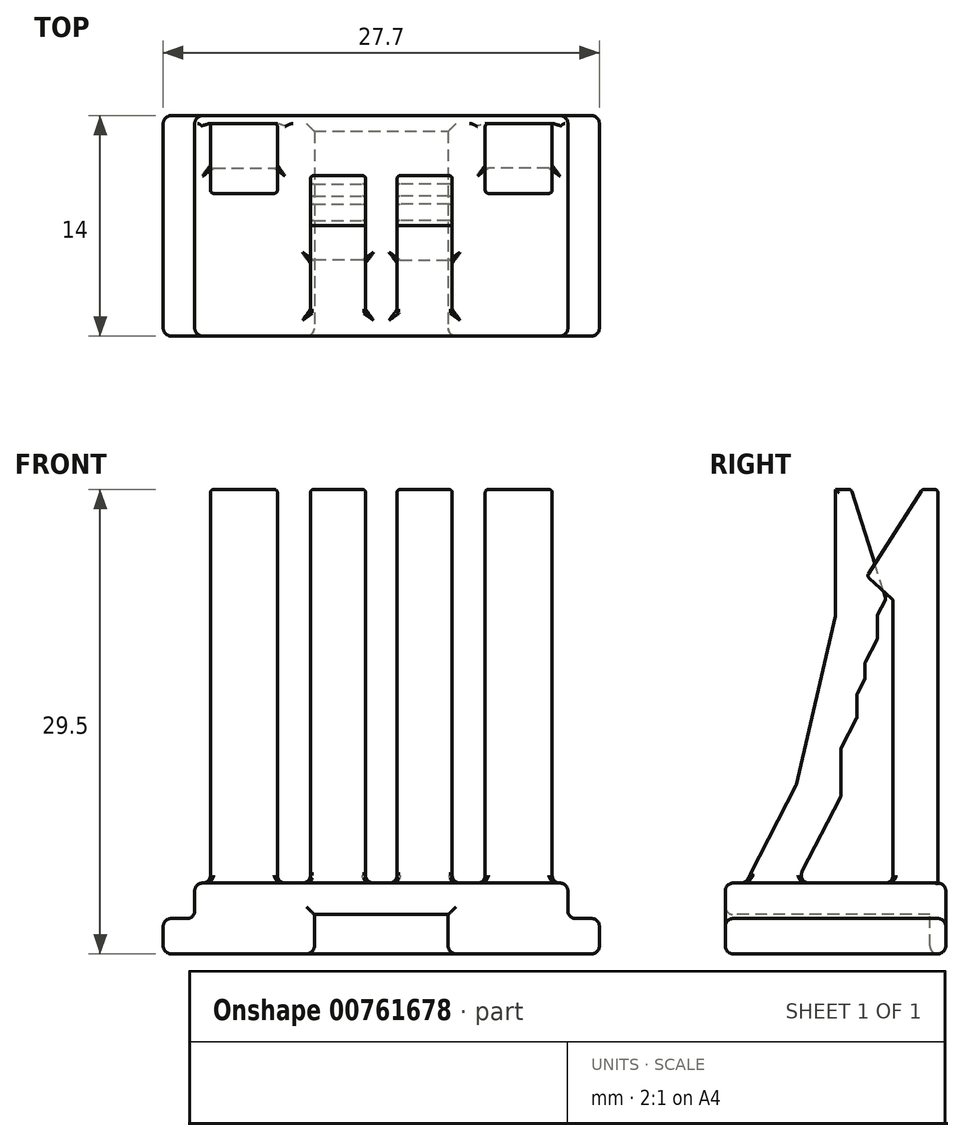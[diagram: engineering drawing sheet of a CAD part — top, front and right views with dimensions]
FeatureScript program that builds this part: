
annotation { "Feature Type Name" : "Feature", "Feature Type Description" : "" }
export const myFeature = defineFeature(function(context is Context, id is Id, definition is map)
    precondition{}
    {
        {
            var Q0;
            Q0=qCreatedBy(makeId("Front.planeOp"),FACE);
            var sketch = newSketch(context, id + "F0", { "sketchPlane" : qUnion([Q0])});
            skLineSegment(sketch, "E0.bottom", {"start": v(-13.85, -2.25) * mm, "end": v(13.85, -2.25) * mm});
            skLineSegment(sketch, "E0.top", {"start": v(-13.85, 2.25) * mm, "end": v(13.85, 2.25) * mm});
            skLineSegment(sketch, "E0.left", {"start": v(-13.85, -2.25) * mm, "end": v(-13.85, 2.25) * mm});
            skLineSegment(sketch, "E0.right", {"start": v(13.85, -2.25) * mm, "end": v(13.85, 2.25) * mm});
            skLineSegment(sketch, "E1", {"start": v(0, 2.25) * mm, "end": v(0, -2.25) * mm, "construction": true});
            skSolve(sketch);
        }
        {
            var Q0;
            Q0 = qSketchRegion(id + "F0", true);
            extrude(context, id + "F1", {"entities" : qUnion([Q0]), "endBound" : BoundingType.SYMMETRIC, "depth" : 14 * mm, "offsetDistance" : 25 * mm});
        }
        {
            var Q0;
            Q0=makeQuery(id+"F1.opExtrude","CAP_FACE",FACE,{"disambiguationData":[OSD([sQuery(id+"F0.wireOp",EDGE,"E0.bottom"),sQuery(id+"F0.wireOp",EDGE,"E0.top"),sQuery(id+"F0.wireOp",EDGE,"E0.left"),sQuery(id+"F0.wireOp",EDGE,"E0.right")])],"isStart":false});
            var sketch = newSketch(context, id + "F2", { "sketchPlane" : qUnion([Q0])});
            skLineSegment(sketch, "E2.bottom", {"start": v(-4.25, -2.25) * mm, "end": v(4.25, -2.25) * mm});
            skLineSegment(sketch, "E2.top", {"start": v(-4.25, 0.25) * mm, "end": v(4.25, 0.25) * mm});
            skLineSegment(sketch, "E2.left", {"start": v(-4.25, -2.25) * mm, "end": v(-4.25, 0.25) * mm});
            skLineSegment(sketch, "E2.right", {"start": v(4.25, -2.25) * mm, "end": v(4.25, 0.25) * mm});
            skSolve(sketch);
        }
        {
            var Q0;
            Q0 = qSketchRegion(id + "F2", true);
            extrude(context, id + "F3", {"entities" : qUnion([Q0]), "operationType" : NewBodyOperationType.REMOVE, "oppositeDirection" : true, "depth" : 13 * mm, "offsetDistance" : 25 * mm});
        }
        {
            var Q0;
            Q0=makeQuery(id+"F1.opExtrude","CAP_FACE",FACE,{"disambiguationData":[OSD([sQuery(id+"F0.wireOp",EDGE,"E0.bottom"),sQuery(id+"F0.wireOp",EDGE,"E0.top"),sQuery(id+"F0.wireOp",EDGE,"E0.left"),sQuery(id+"F0.wireOp",EDGE,"E0.right")])],"isStart":false});
            var sketch = newSketch(context, id + "F4", { "sketchPlane" : qUnion([Q0])});
            skLineSegment(sketch, "E3.bottom", {"start": v(-13.85, 2.25) * mm, "end": v(-11.85, 2.25) * mm});
            skLineSegment(sketch, "E3.top", {"start": v(-13.85, 0) * mm, "end": v(-11.85, 0) * mm});
            skLineSegment(sketch, "E3.left", {"start": v(-13.85, 2.25) * mm, "end": v(-13.85, 0) * mm});
            skLineSegment(sketch, "E3.right", {"start": v(-11.85, 2.25) * mm, "end": v(-11.85, 0) * mm});
            skLineSegment(sketch, "E4.bottom", {"start": v(13.85, 2.25) * mm, "end": v(11.85, 2.25) * mm});
            skLineSegment(sketch, "E4.top", {"start": v(13.85, 0) * mm, "end": v(11.85, 0) * mm});
            skLineSegment(sketch, "E4.left", {"start": v(13.85, 2.25) * mm, "end": v(13.85, 0) * mm});
            skLineSegment(sketch, "E4.right", {"start": v(11.85, 2.25) * mm, "end": v(11.85, 0) * mm});
            skSolve(sketch);
        }
        {
            var Q0;
            Q0 = qSketchRegion(id + "F4", true);
            extrude(context, id + "F5", {"entities" : qUnion([Q0]), "operationType" : NewBodyOperationType.REMOVE, "endBound" : BoundingType.UP_TO_NEXT, "oppositeDirection" : true, "depth" : 25 * mm, "offsetDistance" : 25 * mm});
        }
        {
            var Q0;
            Q0=qCreatedBy(makeId("Right.planeOp"),FACE);
            cPlane(context, id + "F6", {"entities" : qUnion([Q0]), "cplaneType" : CPlaneType.OFFSET, "offset" : 6.6 * mm, "width" : 150 * mm, "height" : 150 * mm});
        }
        {
            var Q0;
            Q0=qCreatedBy(id+"F6.planeOp",FACE);
            var sketch = newSketch(context, id + "F7", { "sketchPlane" : qUnion([Q0])});
            skLineSegment(sketch, "E5.bottom", {"start": v(6.5, 2.25) * mm, "end": v(3.65, 2.25) * mm});
            skLineSegment(sketch, "E5.left", {"start": v(6.5, 2.25) * mm, "end": v(6.5, 27.25) * mm});
            skLineSegment(sketch, "E5.right", {"start": v(3.65, 2.25) * mm, "end": v(3.65, 20.25) * mm});
            skLineSegment(sketch, "E6", {"start": v(3.65, 20.25) * mm, "end": v(2, 21.75) * mm});
            skLineSegment(sketch, "E7", {"start": v(2, 21.75) * mm, "end": v(5.5, 27.25) * mm});
            skLineSegment(sketch, "E8", {"start": v(5.5, 27.25) * mm, "end": v(6.5, 27.25) * mm});
            skSolve(sketch);
        }
        {
            var Q0;
            Q0 = qSketchRegion(id + "F7", true);
            extrude(context, id + "F8", {"entities" : qUnion([Q0]), "depth" : 4.25 * mm, "offsetDistance" : 25 * mm});
        }
        {
            var Q0;
            Q0=qCreatedBy(makeId("Right.planeOp"),FACE);
            cPlane(context, id + "F9", {"entities" : qUnion([Q0]), "cplaneType" : CPlaneType.OFFSET, "offset" : 1 * mm, "width" : 150 * mm, "height" : 150 * mm});
        }
        {
            var Q0;
            Q0=qCreatedBy(id+"F9.planeOp",FACE);
            var sketch = newSketch(context, id + "F10", { "sketchPlane" : qUnion([Q0])});
            skLineSegment(sketch, "E9", {"start": v(1.36, 12.75) * mm, "end": v(0.33, 10.75) * mm});
            skLineSegment(sketch, "E10", {"start": v(0.33, 10.75) * mm, "end": v(0.33, 7.75) * mm});
            skLineSegment(sketch, "E11", {"start": v(0.33, 7.75) * mm, "end": v(-2.5, 2.25) * mm});
            skLineSegment(sketch, "E12", {"start": v(-2.5, 2.25) * mm, "end": v(-5.7, 2.25) * mm});
            skLineSegment(sketch, "E13", {"start": v(-5.7, 2.25) * mm, "end": v(-2.5, 8.48) * mm});
            skLineSegment(sketch, "E14", {"start": v(1.36, 12.75) * mm, "end": v(1.36, 14.25) * mm});
            skLineSegment(sketch, "E15", {"start": v(1.36, 14.25) * mm, "end": v(1.88, 15.25) * mm});
            skLineSegment(sketch, "E16", {"start": v(1.88, 15.25) * mm, "end": v(1.88, 16.25) * mm});
            skLineSegment(sketch, "E17", {"start": v(1.88, 16.25) * mm, "end": v(2.65, 17.75) * mm});
            skLineSegment(sketch, "E18", {"start": v(2.65, 17.75) * mm, "end": v(2.65, 19.25) * mm});
            skLineSegment(sketch, "E19", {"start": v(2.65, 19.25) * mm, "end": v(3.2, 20.32) * mm});
            skLineSegment(sketch, "E20", {"start": v(3.2, 20.32) * mm, "end": v(1, 27.25) * mm});
            skLineSegment(sketch, "E21", {"start": v(1, 27.25) * mm, "end": v(0, 27.25) * mm});
            skLineSegment(sketch, "E22", {"start": v(0, 27.25) * mm, "end": v(0, 19.25) * mm});
            skLineSegment(sketch, "E23", {"start": v(0, 19.25) * mm, "end": v(-2.5, 8.48) * mm});
            skSolve(sketch);
        }
        {
            var Q0;
            Q0 = qSketchRegion(id + "F10", true);
            extrude(context, id + "F11", {"entities" : qUnion([Q0]), "depth" : 3.5 * mm, "offsetDistance" : 25 * mm});
        }
        {
            var Q0;
            Q0=makeQuery(id+"F1.opExtrude","CAP_FACE",FACE,{"disambiguationData":[OSD([sQuery(id+"F0.wireOp",EDGE,"E0.bottom"),sQuery(id+"F0.wireOp",EDGE,"E0.top"),sQuery(id+"F0.wireOp",EDGE,"E0.left"),sQuery(id+"F0.wireOp",EDGE,"E0.right")])],"isStart":false});
            var Q1;
            Q1=makeQuery(id+"F1.opExtrude","CAP_FACE",FACE,{"disambiguationData":[OSD([sQuery(id+"F0.wireOp",EDGE,"E0.bottom"),sQuery(id+"F0.wireOp",EDGE,"E0.top"),sQuery(id+"F0.wireOp",EDGE,"E0.left"),sQuery(id+"F0.wireOp",EDGE,"E0.right")])],"isStart":true});
            var Q2;
            Q2=makeQuery(id+"F1.opExtrude","SWEPT_FACE",FACE,{"disambiguationData":[OSD([sQuery(id+"F0.wireOp",EDGE,"E0.top")])]});
            var Q3;
            Q3=makeQuery(id+"F1.opExtrude","SWEPT_FACE",FACE,{"disambiguationData":[OSD([sQuery(id+"F0.wireOp",EDGE,"E0.bottom")])]});
            var Q4;
            Q4=makeQuery(id+"F5.boolean.opBoolean","COPY",FACE,{"derivedFrom":makeQuery(id+"F5.opExtrude","SWEPT_FACE",FACE,{"disambiguationData":[OSD([sQuery(id+"F4.wireOp",EDGE,"E3.top")])]})});
            var Q5;
            Q5=makeQuery(id+"F5.boolean.opBoolean","COPY",FACE,{"derivedFrom":makeQuery(id+"F5.opExtrude","SWEPT_FACE",FACE,{"disambiguationData":[OSD([sQuery(id+"F4.wireOp",EDGE,"E4.top")])]})});
            fillet(context, id + "F12", {"entities" : qUnion([Q0, Q1, Q2, Q3, Q4, Q5]), "radius" : 0.5 * mm, "tangentPropagation" : true, "allowEdgeOverflow" : false});
        }
        {
            var Q0;
            Q0=makeQuery(id+"F8.opExtrude","SWEPT_BODY",BODY,{"disambiguationData":[OSD([sQuery(id+"F7.wireOp",EDGE,"E5.bottom"),sQuery(id+"F7.wireOp",EDGE,"E5.left"),sQuery(id+"F7.wireOp",EDGE,"E5.right"),sQuery(id+"F7.wireOp",EDGE,"E6"),sQuery(id+"F7.wireOp",EDGE,"E7"),sQuery(id+"F7.wireOp",EDGE,"E8")])]});
            var Q1;
            Q1=makeQuery(id+"F11.opExtrude","SWEPT_BODY",BODY,{"disambiguationData":[OSD([sQuery(id+"F10.wireOp",EDGE,"E9"),sQuery(id+"F10.wireOp",EDGE,"E10"),sQuery(id+"F10.wireOp",EDGE,"E11"),sQuery(id+"F10.wireOp",EDGE,"E12"),sQuery(id+"F10.wireOp",EDGE,"E13"),sQuery(id+"F10.wireOp",EDGE,"E14"),sQuery(id+"F10.wireOp",EDGE,"E15"),sQuery(id+"F10.wireOp",EDGE,"E16"),sQuery(id+"F10.wireOp",EDGE,"E17"),sQuery(id+"F10.wireOp",EDGE,"E18"),sQuery(id+"F10.wireOp",EDGE,"E19"),sQuery(id+"F10.wireOp",EDGE,"E20"),sQuery(id+"F10.wireOp",EDGE,"E21"),sQuery(id+"F10.wireOp",EDGE,"E22"),sQuery(id+"F10.wireOp",EDGE,"E23")])]});
            var Q2;
            Q2=qCreatedBy(makeId("Right.planeOp"),FACE);
            mirror(context, id + "F13", {"operationType" : NewBodyOperationType.ADD, "entities" : qUnion([Q0, Q1]), "mirrorPlane" : qUnion([Q2])});
        }
        {
            var Q0;
            Q0=makeQuery(id+"F1.opExtrude","SWEPT_FACE",FACE,{"disambiguationData":[OSD([sQuery(id+"F0.wireOp",EDGE,"E0.top")])]});
            fillet(context, id + "F14", {"entities" : qUnion([Q0]), "radius" : 0.5 * mm, "tangentPropagation" : true, "allowEdgeOverflow" : false});
        }
        {
            var Q0;
            Q0=makeQuery(id+"F8.opExtrude","SWEPT_FACE",FACE,{"disambiguationData":[OSD([sQuery(id+"F7.wireOp",EDGE,"E5.right")])]});
            var Q1;
            Q1=makeQuery(id+"F8.opExtrude","SWEPT_FACE",FACE,{"disambiguationData":[OSD([sQuery(id+"F7.wireOp",EDGE,"E7")])]});
            var Q2;
            Q2=makeQuery(id+"F11.opExtrude","CAP_FACE",FACE,{"disambiguationData":[OSD([sQuery(id+"F10.wireOp",EDGE,"E9"),sQuery(id+"F10.wireOp",EDGE,"E10"),sQuery(id+"F10.wireOp",EDGE,"E11"),sQuery(id+"F10.wireOp",EDGE,"E12"),sQuery(id+"F10.wireOp",EDGE,"E13"),sQuery(id+"F10.wireOp",EDGE,"E14"),sQuery(id+"F10.wireOp",EDGE,"E15"),sQuery(id+"F10.wireOp",EDGE,"E16"),sQuery(id+"F10.wireOp",EDGE,"E17"),sQuery(id+"F10.wireOp",EDGE,"E18"),sQuery(id+"F10.wireOp",EDGE,"E19"),sQuery(id+"F10.wireOp",EDGE,"E20"),sQuery(id+"F10.wireOp",EDGE,"E21"),sQuery(id+"F10.wireOp",EDGE,"E22"),sQuery(id+"F10.wireOp",EDGE,"E23")])],"isStart":true});
            var Q3;
            Q3=makeQuery(id+"F8.opExtrude","CAP_FACE",FACE,{"disambiguationData":[OSD([sQuery(id+"F7.wireOp",EDGE,"E5.bottom"),sQuery(id+"F7.wireOp",EDGE,"E5.left"),sQuery(id+"F7.wireOp",EDGE,"E5.right"),sQuery(id+"F7.wireOp",EDGE,"E6"),sQuery(id+"F7.wireOp",EDGE,"E7"),sQuery(id+"F7.wireOp",EDGE,"E8")])],"isStart":true});
            var Q4;
            Q4=makeQuery(id+"F8.opExtrude","CAP_FACE",FACE,{"disambiguationData":[OSD([sQuery(id+"F7.wireOp",EDGE,"E5.bottom"),sQuery(id+"F7.wireOp",EDGE,"E5.left"),sQuery(id+"F7.wireOp",EDGE,"E5.right"),sQuery(id+"F7.wireOp",EDGE,"E6"),sQuery(id+"F7.wireOp",EDGE,"E7"),sQuery(id+"F7.wireOp",EDGE,"E8")])],"isStart":false});
            var Q5;
            Q5=makeQuery(id+"F8.opExtrude","SWEPT_EDGE",EDGE,{"disambiguationData":[OSD([sQuery(id+"F7.wireOp",EDGE,"E5.left"),sQuery(id+"F7.wireOp",EDGE,"E8")])]});
            var Q6;
            Q6=makeQuery(id+"F11.opExtrude","CAP_FACE",FACE,{"disambiguationData":[OSD([sQuery(id+"F10.wireOp",EDGE,"E9"),sQuery(id+"F10.wireOp",EDGE,"E10"),sQuery(id+"F10.wireOp",EDGE,"E11"),sQuery(id+"F10.wireOp",EDGE,"E12"),sQuery(id+"F10.wireOp",EDGE,"E13"),sQuery(id+"F10.wireOp",EDGE,"E14"),sQuery(id+"F10.wireOp",EDGE,"E15"),sQuery(id+"F10.wireOp",EDGE,"E16"),sQuery(id+"F10.wireOp",EDGE,"E17"),sQuery(id+"F10.wireOp",EDGE,"E18"),sQuery(id+"F10.wireOp",EDGE,"E19"),sQuery(id+"F10.wireOp",EDGE,"E20"),sQuery(id+"F10.wireOp",EDGE,"E21"),sQuery(id+"F10.wireOp",EDGE,"E22"),sQuery(id+"F10.wireOp",EDGE,"E23")])],"isStart":false});
            var Q7;
            Q7=makeQuery(id+"F11.opExtrude","SWEPT_FACE",FACE,{"disambiguationData":[OSD([sQuery(id+"F10.wireOp",EDGE,"E23")])]});
            var Q8;
            Q8=makeQuery(id+"F11.opExtrude","SWEPT_FACE",FACE,{"disambiguationData":[OSD([sQuery(id+"F10.wireOp",EDGE,"E20")])]});
            var Q9;
            Q9=makeQuery(id+"F11.opExtrude","SWEPT_FACE",FACE,{"disambiguationData":[OSD([sQuery(id+"F10.wireOp",EDGE,"E18")])]});
            var Q10;
            Q10=makeQuery(id+"F11.opExtrude","SWEPT_FACE",FACE,{"disambiguationData":[OSD([sQuery(id+"F10.wireOp",EDGE,"E16")])]});
            var Q11;
            Q11=makeQuery(id+"F11.opExtrude","SWEPT_FACE",FACE,{"disambiguationData":[OSD([sQuery(id+"F10.wireOp",EDGE,"E14")])]});
            var Q12;
            Q12=makeQuery(id+"F11.opExtrude","SWEPT_FACE",FACE,{"disambiguationData":[OSD([sQuery(id+"F10.wireOp",EDGE,"E10")])]});
            var Q13;
            Q13=makeQuery(id+"F13.opPattern","COPY",FACE,{"derivedFrom":makeQuery(id+"F11.opExtrude","SWEPT_FACE",FACE,{"disambiguationData":[OSD([sQuery(id+"F10.wireOp",EDGE,"E10")])]}),"instanceName":"1"});
            var Q14;
            Q14=makeQuery(id+"F13.opPattern","COPY",FACE,{"derivedFrom":makeQuery(id+"F11.opExtrude","SWEPT_FACE",FACE,{"disambiguationData":[OSD([sQuery(id+"F10.wireOp",EDGE,"E14")])]}),"instanceName":"1"});
            var Q15;
            Q15=makeQuery(id+"F13.opPattern","COPY",FACE,{"derivedFrom":makeQuery(id+"F11.opExtrude","SWEPT_FACE",FACE,{"disambiguationData":[OSD([sQuery(id+"F10.wireOp",EDGE,"E16")])]}),"instanceName":"1"});
            var Q16;
            Q16=makeQuery(id+"F13.opPattern","COPY",FACE,{"derivedFrom":makeQuery(id+"F11.opExtrude","SWEPT_FACE",FACE,{"disambiguationData":[OSD([sQuery(id+"F10.wireOp",EDGE,"E18")])]}),"instanceName":"1"});
            var Q17;
            Q17=makeQuery(id+"F13.opPattern","COPY",FACE,{"derivedFrom":makeQuery(id+"F11.opExtrude","SWEPT_FACE",FACE,{"disambiguationData":[OSD([sQuery(id+"F10.wireOp",EDGE,"E20")])]}),"instanceName":"1"});
            var Q18;
            Q18=makeQuery(id+"F13.opPattern","COPY",FACE,{"derivedFrom":makeQuery(id+"F8.opExtrude","CAP_FACE",FACE,{"disambiguationData":[OSD([sQuery(id+"F7.wireOp",EDGE,"E5.bottom"),sQuery(id+"F7.wireOp",EDGE,"E5.left"),sQuery(id+"F7.wireOp",EDGE,"E5.right"),sQuery(id+"F7.wireOp",EDGE,"E6"),sQuery(id+"F7.wireOp",EDGE,"E7"),sQuery(id+"F7.wireOp",EDGE,"E8")])],"isStart":false}),"instanceName":"1"});
            var Q19;
            Q19=makeQuery(id+"F13.opPattern","COPY",FACE,{"derivedFrom":makeQuery(id+"F8.opExtrude","CAP_FACE",FACE,{"disambiguationData":[OSD([sQuery(id+"F7.wireOp",EDGE,"E5.bottom"),sQuery(id+"F7.wireOp",EDGE,"E5.left"),sQuery(id+"F7.wireOp",EDGE,"E5.right"),sQuery(id+"F7.wireOp",EDGE,"E6"),sQuery(id+"F7.wireOp",EDGE,"E7"),sQuery(id+"F7.wireOp",EDGE,"E8")])],"isStart":true}),"instanceName":"1"});
            var Q20;
            Q20=makeQuery(id+"F13.opPattern","COPY",FACE,{"derivedFrom":makeQuery(id+"F11.opExtrude","CAP_FACE",FACE,{"disambiguationData":[OSD([sQuery(id+"F10.wireOp",EDGE,"E9"),sQuery(id+"F10.wireOp",EDGE,"E10"),sQuery(id+"F10.wireOp",EDGE,"E11"),sQuery(id+"F10.wireOp",EDGE,"E12"),sQuery(id+"F10.wireOp",EDGE,"E13"),sQuery(id+"F10.wireOp",EDGE,"E14"),sQuery(id+"F10.wireOp",EDGE,"E15"),sQuery(id+"F10.wireOp",EDGE,"E16"),sQuery(id+"F10.wireOp",EDGE,"E17"),sQuery(id+"F10.wireOp",EDGE,"E18"),sQuery(id+"F10.wireOp",EDGE,"E19"),sQuery(id+"F10.wireOp",EDGE,"E20"),sQuery(id+"F10.wireOp",EDGE,"E21"),sQuery(id+"F10.wireOp",EDGE,"E22"),sQuery(id+"F10.wireOp",EDGE,"E23")])],"isStart":true}),"instanceName":"1"});
            var Q21;
            Q21=makeQuery(id+"F13.opPattern","COPY",FACE,{"derivedFrom":makeQuery(id+"F11.opExtrude","CAP_FACE",FACE,{"disambiguationData":[OSD([sQuery(id+"F10.wireOp",EDGE,"E9"),sQuery(id+"F10.wireOp",EDGE,"E10"),sQuery(id+"F10.wireOp",EDGE,"E11"),sQuery(id+"F10.wireOp",EDGE,"E12"),sQuery(id+"F10.wireOp",EDGE,"E13"),sQuery(id+"F10.wireOp",EDGE,"E14"),sQuery(id+"F10.wireOp",EDGE,"E15"),sQuery(id+"F10.wireOp",EDGE,"E16"),sQuery(id+"F10.wireOp",EDGE,"E17"),sQuery(id+"F10.wireOp",EDGE,"E18"),sQuery(id+"F10.wireOp",EDGE,"E19"),sQuery(id+"F10.wireOp",EDGE,"E20"),sQuery(id+"F10.wireOp",EDGE,"E21"),sQuery(id+"F10.wireOp",EDGE,"E22"),sQuery(id+"F10.wireOp",EDGE,"E23")])],"isStart":false}),"instanceName":"1"});
            var Q22;
            Q22=makeQuery(id+"F13.opPattern","COPY",FACE,{"derivedFrom":makeQuery(id+"F8.opExtrude","SWEPT_FACE",FACE,{"disambiguationData":[OSD([sQuery(id+"F7.wireOp",EDGE,"E6")])]}),"instanceName":"1"});
            var Q23;
            Q23=makeQuery(id+"F13.opPattern","COPY",FACE,{"derivedFrom":makeQuery(id+"F8.opExtrude","SWEPT_FACE",FACE,{"disambiguationData":[OSD([sQuery(id+"F7.wireOp",EDGE,"E8")])]}),"instanceName":"1"});
            var Q24;
            Q24=makeQuery(id+"F13.opPattern","COPY",FACE,{"derivedFrom":makeQuery(id+"F11.opExtrude","SWEPT_FACE",FACE,{"disambiguationData":[OSD([sQuery(id+"F10.wireOp",EDGE,"E22")])]}),"instanceName":"1"});
            var Q25;
            Q25=makeQuery(id+"F13.opPattern","COPY",EDGE,{"derivedFrom":makeQuery(id+"F11.opExtrude","SWEPT_EDGE",EDGE,{"disambiguationData":[OSD([sQuery(id+"F10.wireOp",EDGE,"E13"),sQuery(id+"F10.wireOp",EDGE,"E23")])]}),"instanceName":"1"});
            fillet(context, id + "F15", {"entities" : qUnion([Q0, Q1, Q2, Q3, Q4, Q5, Q6, Q7, Q8, Q9, Q10, Q11, Q12, Q13, Q14, Q15, Q16, Q17, Q18, Q19, Q20, Q21, Q22, Q23, Q24, Q25]), "radius" : 0.2 * mm, "tangentPropagation" : true, "allowEdgeOverflow" : false});
        }
    });
